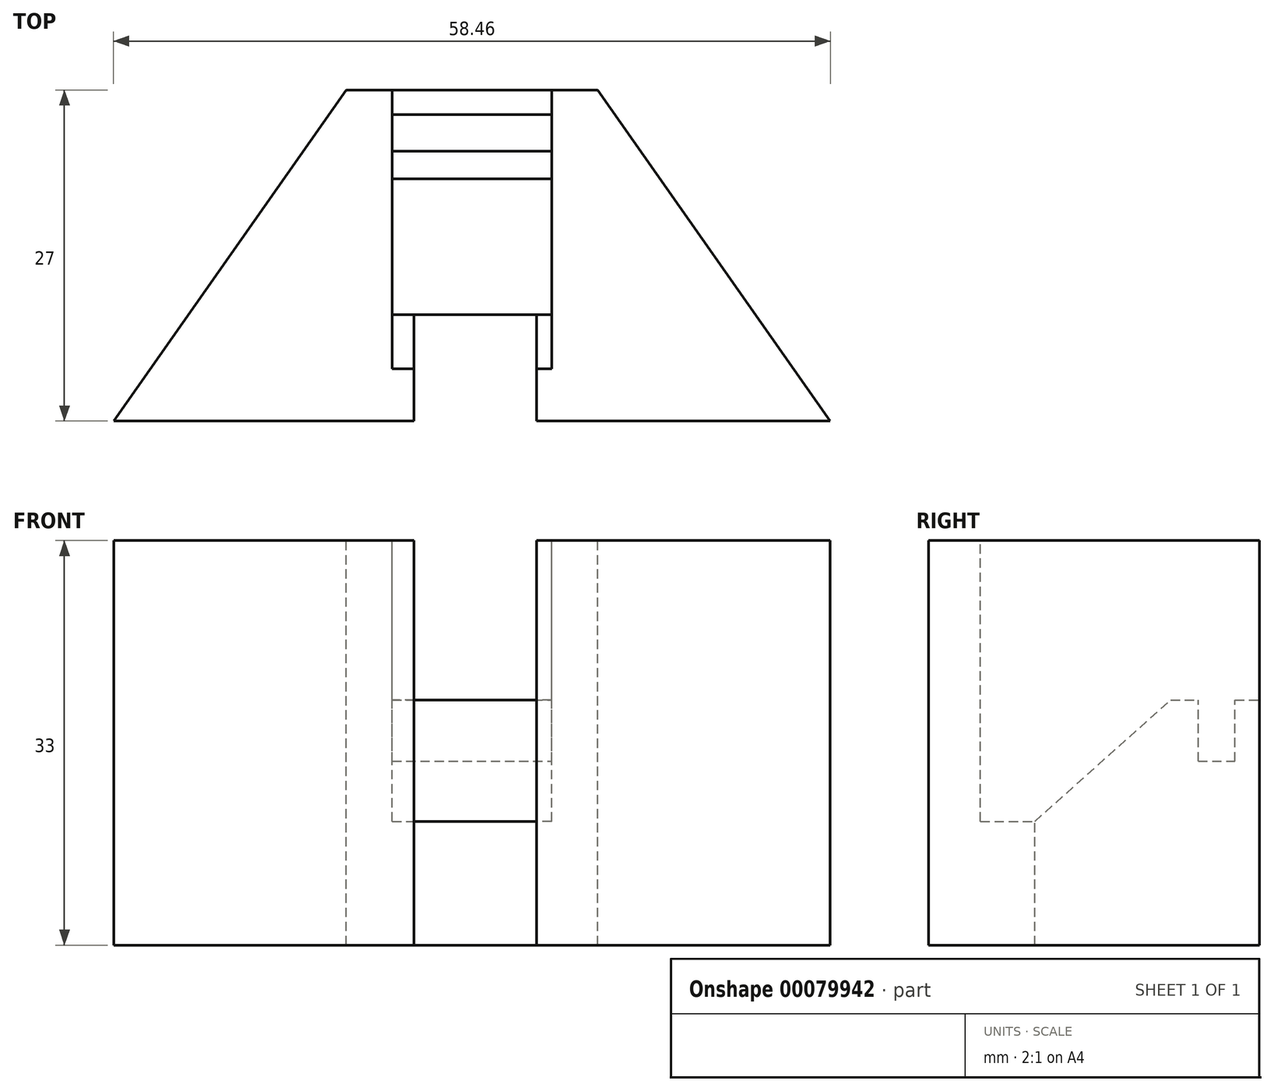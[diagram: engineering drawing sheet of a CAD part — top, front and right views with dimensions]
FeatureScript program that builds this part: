
annotation { "Feature Type Name" : "Feature", "Feature Type Description" : "" }
export const myFeature = defineFeature(function(context is Context, id is Id, definition is map)
    precondition{}
    {
        {
            var Q0;
            Q0=qCreatedBy(makeId("Top.planeOp"),FACE);
            var sketch = newSketch(context, id + "F0", { "sketchPlane" : qUnion([Q0])});
            skLineSegment(sketch, "E0", {"start": v(-29.23, -13.5) * mm, "end": v(-10.25, 13.5) * mm});
            skLineSegment(sketch, "E1", {"start": v(-10.25, 13.5) * mm, "end": v(10.25, 13.5) * mm});
            skLineSegment(sketch, "E2", {"start": v(10.25, 13.5) * mm, "end": v(29.23, -13.5) * mm});
            skLineSegment(sketch, "E3", {"start": v(29.23, -13.5) * mm, "end": v(-29.22, -13.5) * mm});
            skSolve(sketch);
        }
        {
            var Q0;
            Q0 = qSketchRegion(id + "F0", true);
            extrude(context, id + "F1", {"entities" : qUnion([Q0]), "oppositeDirection" : true, "depth" : 33 * mm});
        }
        {
            var Q0;
            Q0=makeQuery(id+"F1.opExtrude","SWEPT_FACE",FACE,{"disambiguationData":[OSD([sQuery(id+"F0.wireOp",EDGE,"E1")])]});
            var sketch = newSketch(context, id + "F2", { "sketchPlane" : qUnion([Q0])});
            skLineSegment(sketch, "E4.bottom", {"start": v(6.5, -13) * mm, "end": v(-6.5, -13) * mm});
            skLineSegment(sketch, "E4.top", {"start": v(6.5, 0) * mm, "end": v(-6.5, 0) * mm});
            skLineSegment(sketch, "E4.left", {"start": v(6.5, -13) * mm, "end": v(6.5, 0) * mm});
            skLineSegment(sketch, "E4.right", {"start": v(-6.5, -13) * mm, "end": v(-6.5, 0) * mm});
            skSolve(sketch);
        }
        {
            var Q0;
            Q0=makeQuery(id+"F2.imprint","IMPRINT",FACE,{"disambiguationData":[TD([[makeQuery(id+"F2.imprint","IMPRINT",EDGE,{"derivedFrom":sQuery(id+"F2.wireOp",EDGE,"E4.bottom")}),-1.0]])]});
            extrude(context, id + "F3", {"entities" : qUnion([Q0]), "operationType" : NewBodyOperationType.REMOVE, "oppositeDirection" : true, "depth" : 22.75 * mm});
        }
        {
            var Q0;
            Q0=makeQuery(id+"F1.opExtrude","CAP_FACE",FACE,{"disambiguationData":[OSD([sQuery(id+"F0.wireOp",EDGE,"E0"),sQuery(id+"F0.wireOp",EDGE,"E1"),sQuery(id+"F0.wireOp",EDGE,"E2"),sQuery(id+"F0.wireOp",EDGE,"E3")])],"isStart":true});
            var sketch = newSketch(context, id + "F4", { "sketchPlane" : qUnion([Q0])});
            skLineSegment(sketch, "E5.bottom", {"start": v(-4.72, -4.83) * mm, "end": v(5.28, -4.83) * mm});
            skLineSegment(sketch, "E5.top", {"start": v(-4.72, -13.5) * mm, "end": v(5.28, -13.5) * mm});
            skLineSegment(sketch, "E5.left", {"start": v(-4.72, -4.83) * mm, "end": v(-4.72, -13.5) * mm});
            skLineSegment(sketch, "E5.right", {"start": v(5.28, -4.83) * mm, "end": v(5.28, -13.5) * mm});
            skSolve(sketch);
        }
        {
            var Q0;
            Q0 = qSketchRegion(id + "F4", true);
            extrude(context, id + "F5", {"entities" : qUnion([Q0]), "operationType" : NewBodyOperationType.REMOVE, "oppositeDirection" : true, "depth" : 33 * mm});
        }
        {
            var Q0;
            Q0=makeQuery(id+"F3.boolean.opBoolean","COPY",FACE,{"derivedFrom":makeQuery(id+"F3.opExtrude","SWEPT_FACE",FACE,{"disambiguationData":[OSD([sQuery(id+"F2.wireOp",EDGE,"E4.bottom")])]})});
            var sketch = newSketch(context, id + "F6", { "sketchPlane" : qUnion([Q0])});
            skLineSegment(sketch, "E6.bottom", {"start": v(-6.5, 11.5) * mm, "end": v(6.5, 11.5) * mm});
            skLineSegment(sketch, "E6.top", {"start": v(-6.5, 8.5) * mm, "end": v(6.5, 8.5) * mm});
            skLineSegment(sketch, "E6.left", {"start": v(-6.5, 11.5) * mm, "end": v(-6.5, 8.5) * mm});
            skLineSegment(sketch, "E6.right", {"start": v(6.5, 11.5) * mm, "end": v(6.5, 8.5) * mm});
            skSolve(sketch);
        }
        {
            var Q0;
            Q0 = qSketchRegion(id + "F6", true);
            extrude(context, id + "F7", {"entities" : qUnion([Q0]), "operationType" : NewBodyOperationType.REMOVE, "oppositeDirection" : true, "depth" : 5 * mm});
        }
        {
            var Q0;
            Q0=qCreatedBy(makeId("Right.planeOp"),FACE);
            var sketch = newSketch(context, id + "F8", { "sketchPlane" : qUnion([Q0])});
            skLineSegment(sketch, "E7", {"start": v(8.5, -11) * mm, "end": v(-9.25, -11) * mm});
            skLineSegment(sketch, "E8", {"start": v(-9.25, -11) * mm, "end": v(-9.25, -22.92) * mm});
            skLineSegment(sketch, "E9", {"start": v(-9.25, -22.92) * mm, "end": v(-4.83, -22.92) * mm});
            skLineSegment(sketch, "E10", {"start": v(-4.83, -22.92) * mm, "end": v(8.5, -11) * mm});
            skLineSegment(sketch, "E11", {"start": v(8.5, -11) * mm, "end": v(8.5, -23.4) * mm, "construction": true});
            skSolve(sketch);
        }
        {
            var Q0;
            Q0 = qSketchRegion(id + "F8", true);
            extrude(context, id + "F9", {"entities" : qUnion([Q0]), "operationType" : NewBodyOperationType.REMOVE, "oppositeDirection" : true, "depth" : 6.5 * mm});
        }
        {
            var Q0;
            Q0 = qSketchRegion(id + "F8", true);
            extrude(context, id + "F10", {"entities" : qUnion([Q0]), "operationType" : NewBodyOperationType.REMOVE, "depth" : 6.5 * mm});
        }
    });
